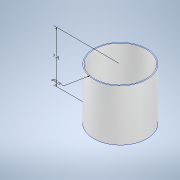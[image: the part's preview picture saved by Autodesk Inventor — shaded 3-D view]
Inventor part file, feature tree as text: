
AUTODESK INVENTOR PART (.ipt)
format: ipt  version: 2022 (Build 260153000, 153)  size: 150,016 bytes
history: native  units: in
note: dims shown in document units (in); Inventor stores cm internally (conversion verified against a paired STEP export)
features: other x4, extrude x3, sketch x3, shell x1, fillet x1
ambient origin geometry x8: Origin, YZ Plane, XZ Plane, XY Plane, X Axis, Y Axis, Z Axis, Center Point
bodies: Solid1 (feature_tree)
feature tree (12):
  other  "Annotations"
  extrude  "Extrusion1"  Depth=0.125in TaperAngle=0.0deg
  shell  "Shell1"  Thickness=0.125in
  extrude  "Extrusion2"  Depth=0.125in TaperAngle=0.0deg
  fillet  "Fillet1"  Radius=0.125in
  sketch  "Sketch1"  dims[d0=7.5in d1=7.25in d2=0.0in d3=0.125in]
  sketch  "Sketch2"  dims[d4=0.125in d5=7.25in d6=0.0in d7=0.125in]
  sketch  "Sketch3"  dims[d11=1.0in d12=0.75in d14=0.0in d15=0.0in d16=0.0in d10=7.25in d17=1.5463in d18=0.3778in d19=0.1355in d20=0.375in d8=7.25in d9=0.5403in]
  other  "Linear Dimension 1"
  other  "Diameter Dimension 1"
  other  "Radial Dimension 1"
  extrude  "Extrusion3"  TaperAngle=0.0deg  [1 undecoded]
note: 1 required parameter value undecoded (feature->parameter linkage not recoverable at this tier; creation-order binding heuristic only, values carry confidence <= 0.55)
